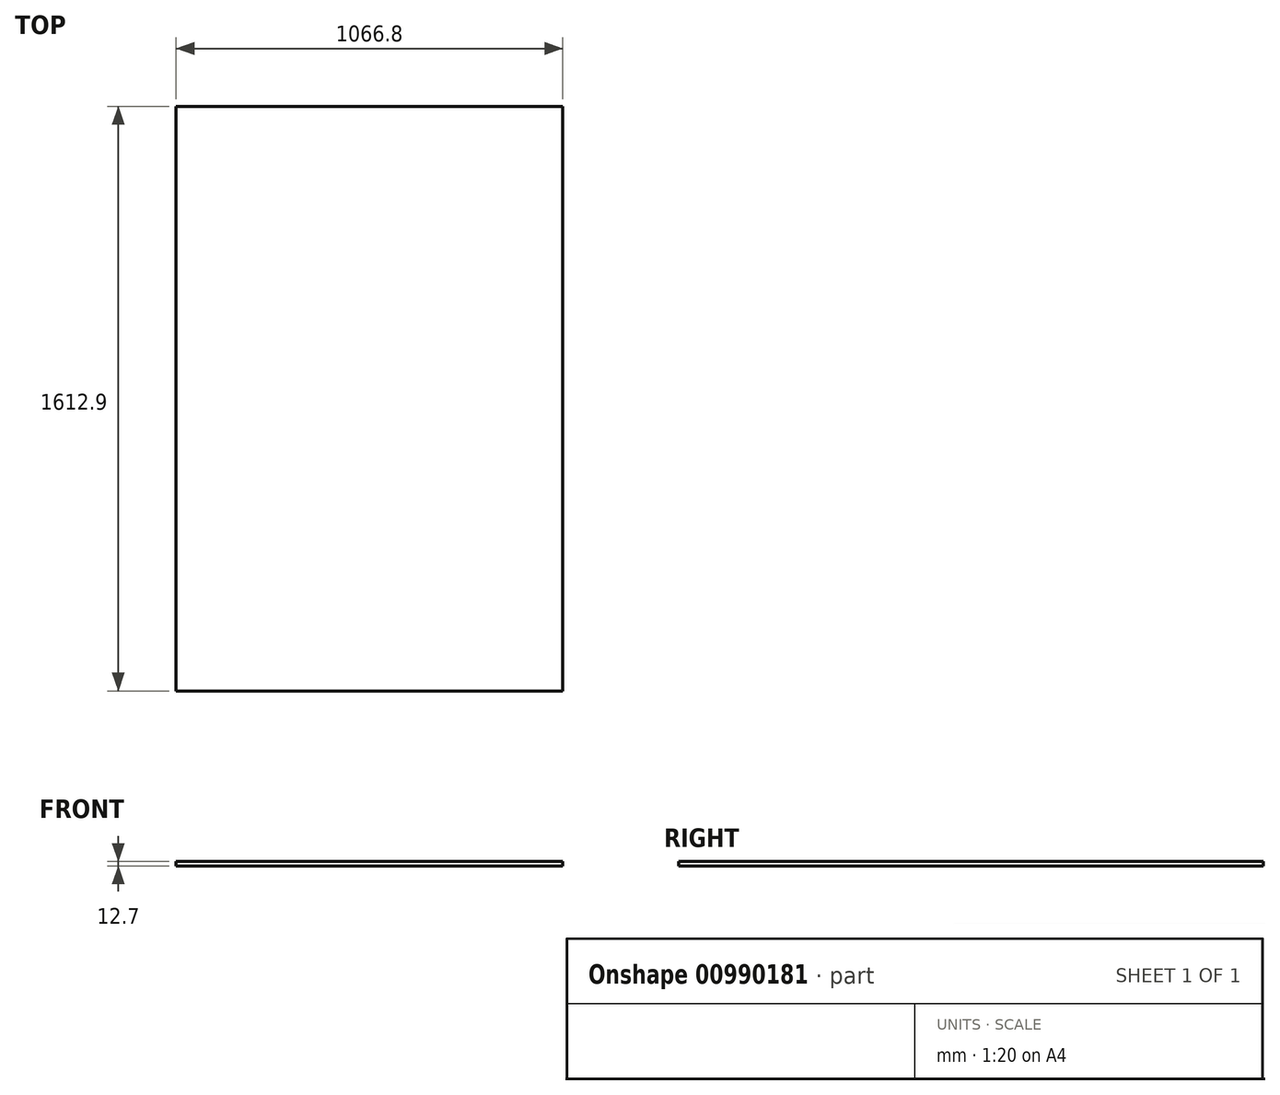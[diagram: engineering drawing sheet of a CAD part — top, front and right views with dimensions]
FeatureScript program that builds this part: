
annotation { "Feature Type Name" : "Feature", "Feature Type Description" : "" }
export const myFeature = defineFeature(function(context is Context, id is Id, definition is map)
    precondition{}
    {
        {
            var Q0;
            Q0=qCreatedBy(makeId("Top.planeOp"),FACE);
            var sketch = newSketch(context, id + "F0", { "sketchPlane" : qUnion([Q0])});
            skLineSegment(sketch, "E0.bottom", {"start": v(533.4, 806.45) * mm, "end": v(-533.4, 806.45) * mm});
            skLineSegment(sketch, "E0.top", {"start": v(533.4, -806.45) * mm, "end": v(-533.4, -806.45) * mm});
            skLineSegment(sketch, "E0.left", {"start": v(533.4, 806.45) * mm, "end": v(533.4, -806.45) * mm});
            skLineSegment(sketch, "E0.right", {"start": v(-533.4, 806.45) * mm, "end": v(-533.4, -806.45) * mm});
            skPoint(sketch, "E0.middle", {"position": v(0, 0) * mm});
            skSolve(sketch);
        }
        {
            var Q0;
            Q0=qSketchRegion(id+"F0",true);
            extrude(context, id + "F1", {"entities" : qUnion([Q0]), "depth" : 12.7 * mm, "offsetDistance" : 25.4 * mm});
        }
    });
